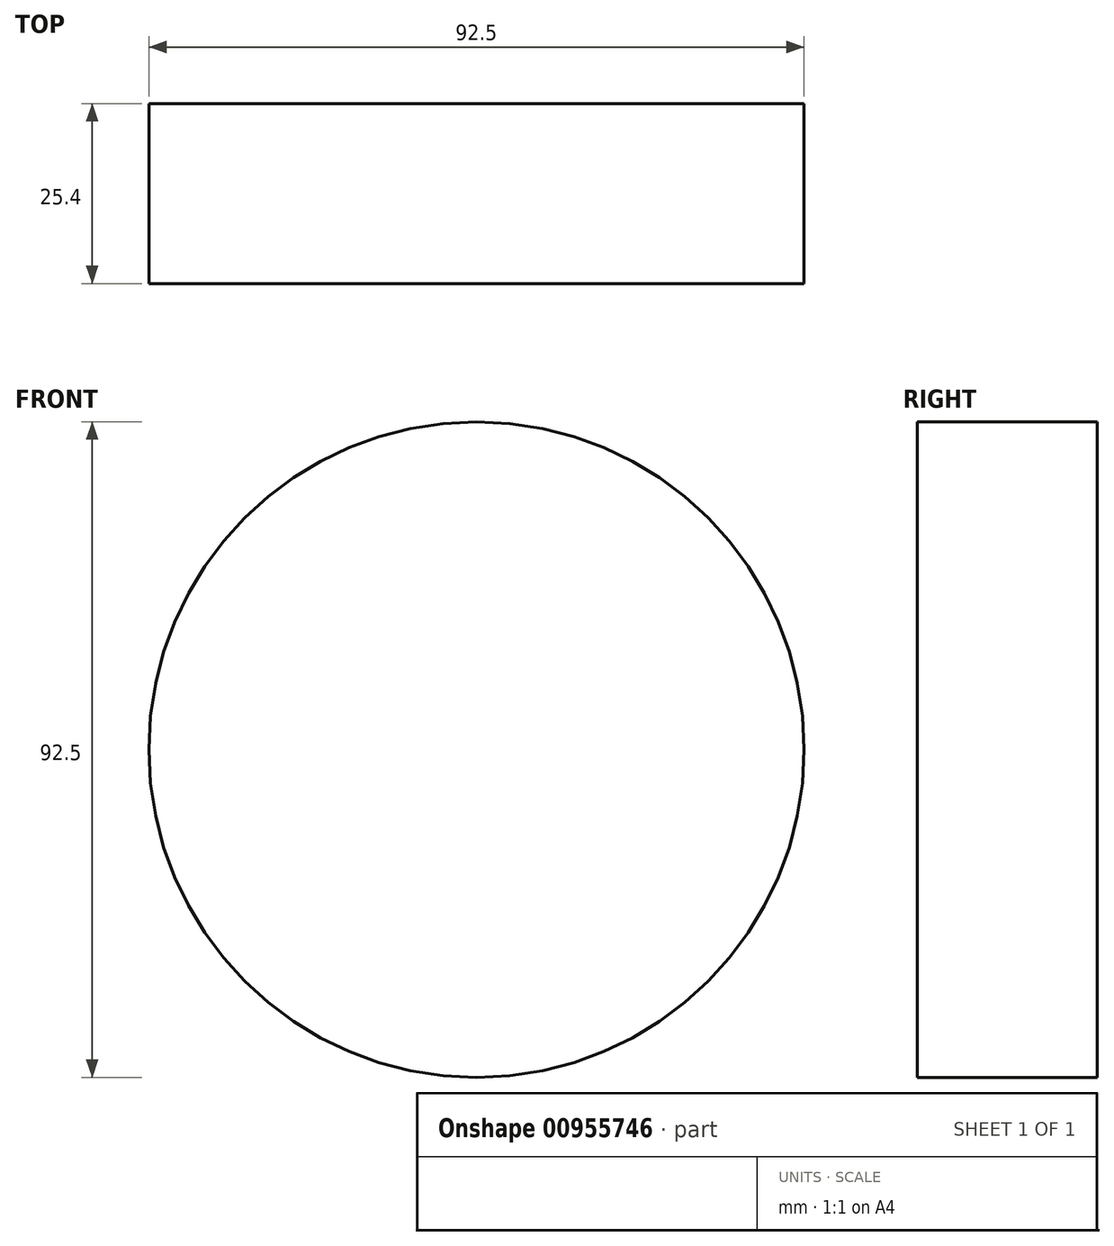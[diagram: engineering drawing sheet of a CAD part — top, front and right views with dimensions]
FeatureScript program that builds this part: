
annotation { "Feature Type Name" : "Feature", "Feature Type Description" : "" }
export const myFeature = defineFeature(function(context is Context, id is Id, definition is map)
    precondition{}
    {
        {
            var Q0;
            Q0=qCreatedBy(makeId("Front.planeOp"),FACE);
            var sketch = newSketch(context, id + "F0", { "sketchPlane" : qUnion([Q0])});
            skCircle(sketch, "E0", {"center": v(0, 0) * mm, "radius": 46.25 * mm});
            skSolve(sketch);
        }
        {
            var Q0;
            Q0 = qSketchRegion(id + "F0", true);
            extrude(context, id + "F1", {"entities" : qUnion([Q0]), "depth" : 25.4 * mm, "offsetDistance" : 25.4 * mm});
        }
    });
